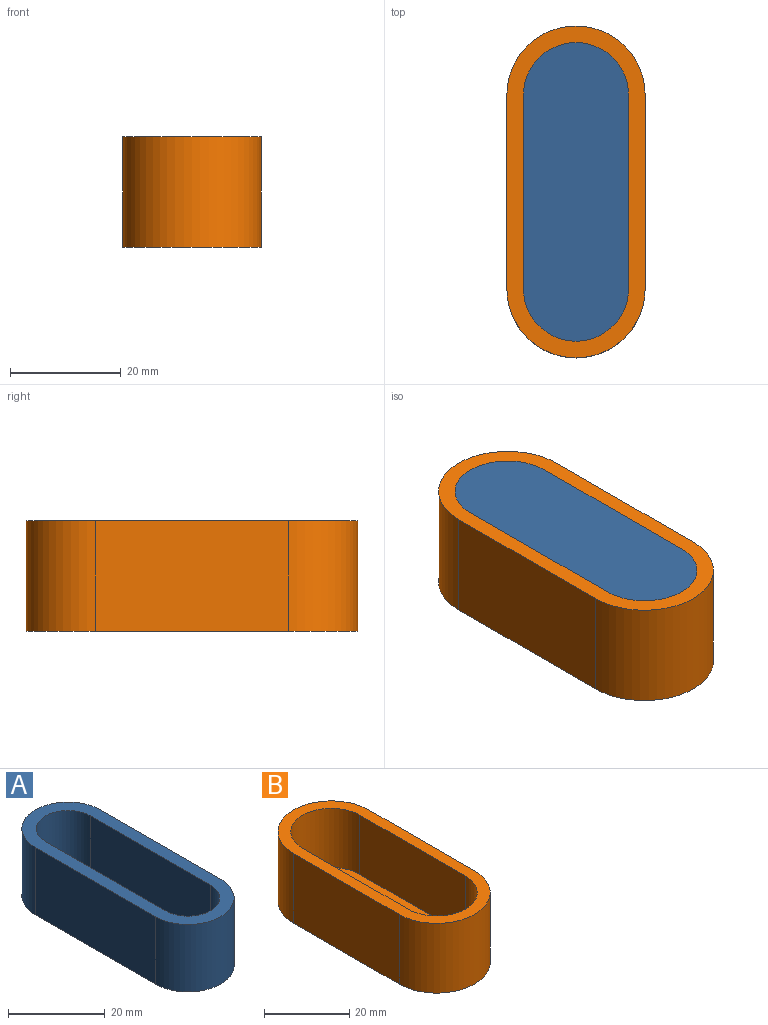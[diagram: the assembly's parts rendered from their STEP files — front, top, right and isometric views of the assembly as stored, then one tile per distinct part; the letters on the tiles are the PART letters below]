
ASSEMBLY  parts=2 mates=1
PART A: 11 faces, bbox 19x54x17 mm
  f0: plane 54x19mm, normal (0,0,-1), area 948.5mm2, adj f5,f6,f7,f8
  f1: plane 35x14mm, normal (1,0,0), area 490mm2, adj f3,f4,f9,f10
  f2: plane 35x14mm, normal (-1,0,0), area 490mm2, adj f3,f4,f9,f10
  f3: cylinder r=6.5mm len=14mm, axis (0,0,-1), area 285.9mm2, adj f1,f2,f9,f10
  f4: cylinder r=6.5mm len=14mm, axis (0,0,-1), area 285.9mm2, adj f1,f2,f9,f10
  f5: cylinder r=9.5mm len=19mm, axis (0,0,-1), area 507.4mm2, adj f0,f6,f8,f9
  f6: plane 35x17mm, normal (-1,0,0), area 595mm2, adj f0,f5,f7,f9
  f7: cylinder r=9.5mm len=19mm, axis (0,0,-1), area 507.4mm2, adj f0,f6,f8,f9
  f8: plane 35x17mm, normal (1,0,0), area 595mm2, adj f0,f5,f7,f9
  f9: plane 54x19mm, normal (0,0,1), area 360.8mm2, adj f1,f2,f3,f4,f5,f6,f7,f8
  f10: plane 48x13mm, normal (0,0,1), area 587.7mm2, adj f1,f2,f3,f4
PART B: 11 faces, bbox 25x60x20 mm
  f0: cylinder r=9.5mm len=19mm, axis (0,0,-1), area 507.4mm2, adj f1,f7,f8,f10
  f1: plane 35x17mm, normal (-1,0,0), area 595mm2, adj f0,f2,f8,f10
  f2: cylinder r=9.5mm len=19mm, axis (0,0,-1), area 507.4mm2, adj f1,f7,f8,f10
  f3: plane 35x20mm, normal (1,0,0), area 700mm2, adj f4,f6,f8,f9
  f4: cylinder r=12.5mm len=25mm, axis (0,0,-1), area 785.4mm2, adj f3,f5,f8,f9
  f5: plane 35x20mm, normal (-1,0,0), area 700mm2, adj f4,f6,f8,f9
  f6: cylinder r=12.5mm len=25mm, axis (0,0,-1), area 785.4mm2, adj f3,f5,f8,f9
  f7: plane 35x17mm, normal (1,0,0), area 595mm2, adj f0,f2,f8,f10
  f8: plane 60x25mm, normal (0,0,1), area 417.3mm2, adj f0,f1,f2,f3,f4,f5,f6,f7
  f9: plane 60x25mm, normal (0,0,-1), area 1365.9mm2, adj f3,f4,f5,f6
  f10: plane 54x19mm, normal (0,0,1), area 948.5mm2, adj f0,f1,f2,f7
PLACE A rot(axis=(1,0,0),180deg) t=(-10.1,-31.04,-67.4)mm
PLACE B t=(-11.65,-26.03,-87.4)mm
MATE slider A.f0 <-> B.f10  axis (0,0,1) through (-28.24,-23.87,-67.4)mm
